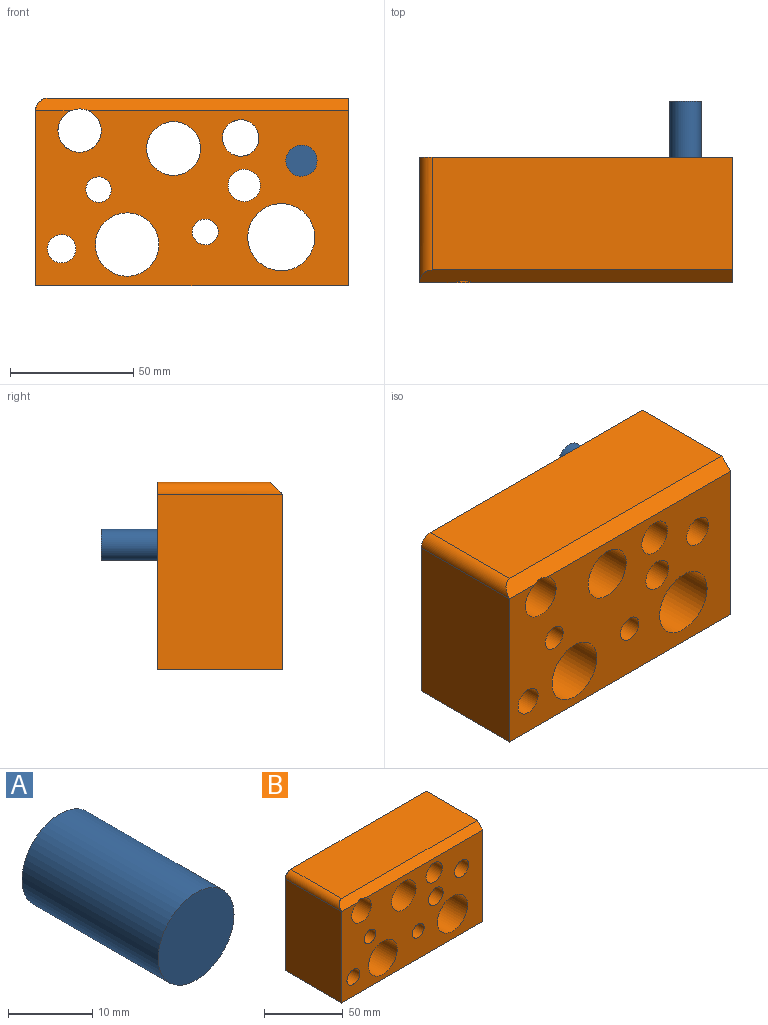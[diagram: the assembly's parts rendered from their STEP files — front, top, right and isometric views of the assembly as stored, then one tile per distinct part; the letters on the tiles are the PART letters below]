
ASSEMBLY  parts=2 mates=1
PART A: 3 faces, bbox 12.7x22.9x12.7 mm
  f0: cylinder r=6.35mm len=22.86mm, axis (0,1,0), area 912.1mm2, adj f1,f2
  f1: plane 12.7x12.7mm, normal (0,-1,0), area 126.7mm2, adj f0
  f2: plane 12.7x12.7mm, normal (0,1,0), area 126.7mm2, adj f0
PART B: 18 faces, bbox 127x50.8x76.2 mm
  f0: plane 71.12x50.8mm, normal (-1,0,0), area 3612.9mm2, adj f1,f13,f14,f17
  f1: plane 127x50.8mm, normal (0,0,-1), area 6451.6mm2, adj f0,f2,f13,f14
  f2: plane 76.2x50.8mm, normal (1,0,0), area 3858.1mm2, adj f1,f12,f13,f14,f16
  f3: cylinder r=6.35mm len=50.8mm, axis (0,1,0), area 2026.8mm2, adj f13,f14
  f4: cylinder r=8.79mm len=50.8mm, axis (0,1,0), area 2803.5mm2, adj f13,f14,f16
  f5: cylinder r=12.86mm len=50.8mm, axis (0,1,0), area 4104.2mm2, adj f13,f14
  f6: cylinder r=13.62mm len=50.8mm, axis (0,1,0), area 4348.4mm2, adj f13,f14
  f7: cylinder r=10.93mm len=50.8mm, axis (0,1,0), area 3487.7mm2, adj f13,f14
  f8: cylinder r=5.18mm len=50.8mm, axis (0,1,0), area 1653.3mm2, adj f13,f14
  f9: cylinder r=6.54mm len=50.8mm, axis (0,1,0), area 2088.4mm2, adj f13,f14
  f10: cylinder r=5.23mm len=50.8mm, axis (0,1,0), area 1670mm2, adj f13,f14
  f11: cylinder r=5.77mm len=50.8mm, axis (0,1,0), area 1840.4mm2, adj f13,f14
  f12: plane 121.92x45.72mm, normal (0,0,1), area 5574.2mm2, adj f2,f14,f16,f17
  f13: plane 127x71.12mm, normal (0,-1,0), area 6607.1mm2, adj f0,f1,f2,f3,f4,f5,f6,f7
  f14: plane 127x76.2mm, normal (0,1,0), area 7243.4mm2, adj f0,f1,f2,f3,f4,f5,f6,f7
  f15: cylinder r=7.4mm len=50.8mm, axis (0,-1,0), area 2362.2mm2, adj f13,f14
  f16: plane 127x5.08mm, normal (0,-0.71,0.71), area 899.9mm2, adj f2,f4,f12,f13,f17
  f17: cylinder r=5.08mm len=50.8mm, axis (0,-1,0), area 379.6mm2, adj f0,f12,f14,f16
PLACE A t=(92.66,22.86,-17.09)mm
PLACE B at identity
MATE fastened A.f0 <-> B.f3  axis (0,-1,0) through (46.45,0,16.42)mm
